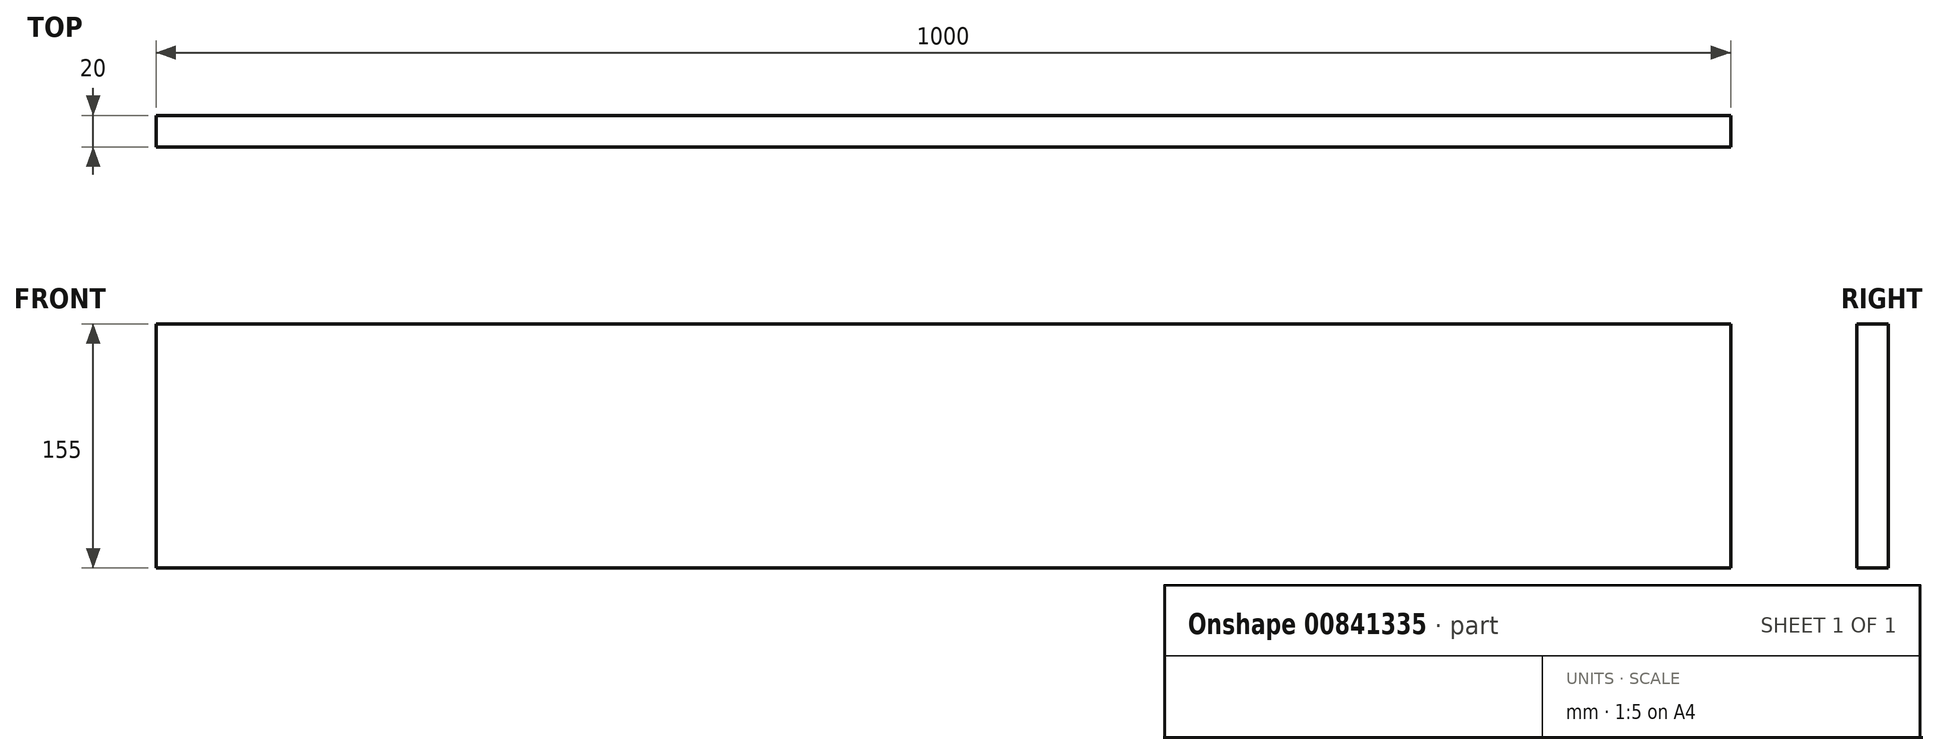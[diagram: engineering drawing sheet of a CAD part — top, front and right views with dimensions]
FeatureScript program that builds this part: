
annotation { "Feature Type Name" : "Feature", "Feature Type Description" : "" }
export const myFeature = defineFeature(function(context is Context, id is Id, definition is map)
    precondition{}
    {
        {
            var Q0;
            Q0=qCreatedBy(makeId("Front.planeOp"),FACE);
            var sketch = newSketch(context, id + "F0", { "sketchPlane" : qUnion([Q0])});
            skLineSegment(sketch, "E0.bottom", {"start": v(-500, -77.5) * mm, "end": v(500, -77.5) * mm});
            skLineSegment(sketch, "E0.top", {"start": v(-500, 77.5) * mm, "end": v(500, 77.5) * mm});
            skLineSegment(sketch, "E0.left", {"start": v(-500, -77.5) * mm, "end": v(-500, 77.5) * mm});
            skLineSegment(sketch, "E0.right", {"start": v(500, -77.5) * mm, "end": v(500, 77.5) * mm});
            skLineSegment(sketch, "E1", {"start": v(-500, 0) * mm, "end": v(500, 0) * mm, "construction": true});
            skSolve(sketch);
        }
        {
            var Q0;
            Q0=qSketchRegion(id+"F0",true);
            extrude(context, id + "F1", {"entities" : qUnion([Q0]), "depth" : 20 * mm, "offsetDistance" : 25 * mm});
        }
    });
